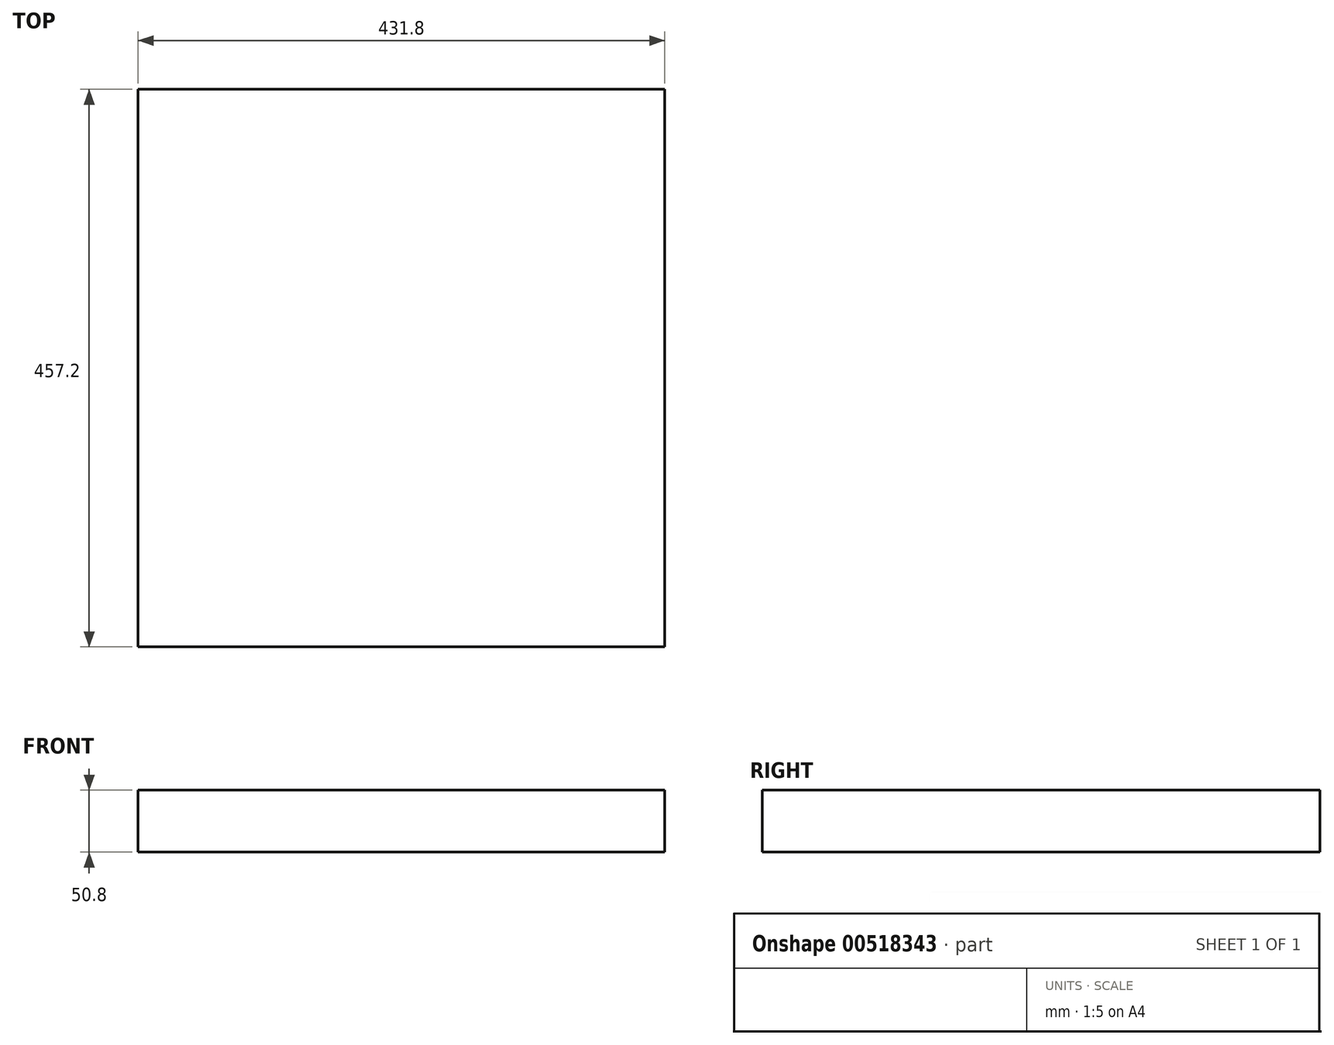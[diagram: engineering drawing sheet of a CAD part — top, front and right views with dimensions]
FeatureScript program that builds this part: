
annotation { "Feature Type Name" : "Feature", "Feature Type Description" : "" }
export const myFeature = defineFeature(function(context is Context, id is Id, definition is map)
    precondition{}
    {
        {
            var Q0;
            Q0=qCreatedBy(makeId("Top.planeOp"),FACE);
            var sketch = newSketch(context, id + "F0", { "sketchPlane" : qUnion([Q0])});
            skLineSegment(sketch, "E0.bottom", {"start": v(-215.9, 228.6) * mm, "end": v(215.9, 228.6) * mm});
            skLineSegment(sketch, "E0.top", {"start": v(-215.9, -228.6) * mm, "end": v(215.9, -228.6) * mm});
            skLineSegment(sketch, "E0.left", {"start": v(-215.9, 228.6) * mm, "end": v(-215.9, -228.6) * mm});
            skLineSegment(sketch, "E0.right", {"start": v(215.9, 228.6) * mm, "end": v(215.9, -228.6) * mm});
            skPoint(sketch, "E0.middle", {"position": v(0, 0) * mm});
            skSolve(sketch);
        }
        {
            var Q0;
            Q0=makeQuery(id+"F0.imprint","IMPRINT",FACE,{"disambiguationData":[TD([[makeQuery(id+"F0.imprint","IMPRINT",EDGE,{"derivedFrom":sQuery(id+"F0.wireOp",EDGE,"E0.bottom")}),-1.0]])]});
            extrude(context, id + "F1", {"entities" : qUnion([Q0]), "depth" : 50.8 * mm});
        }
    });
